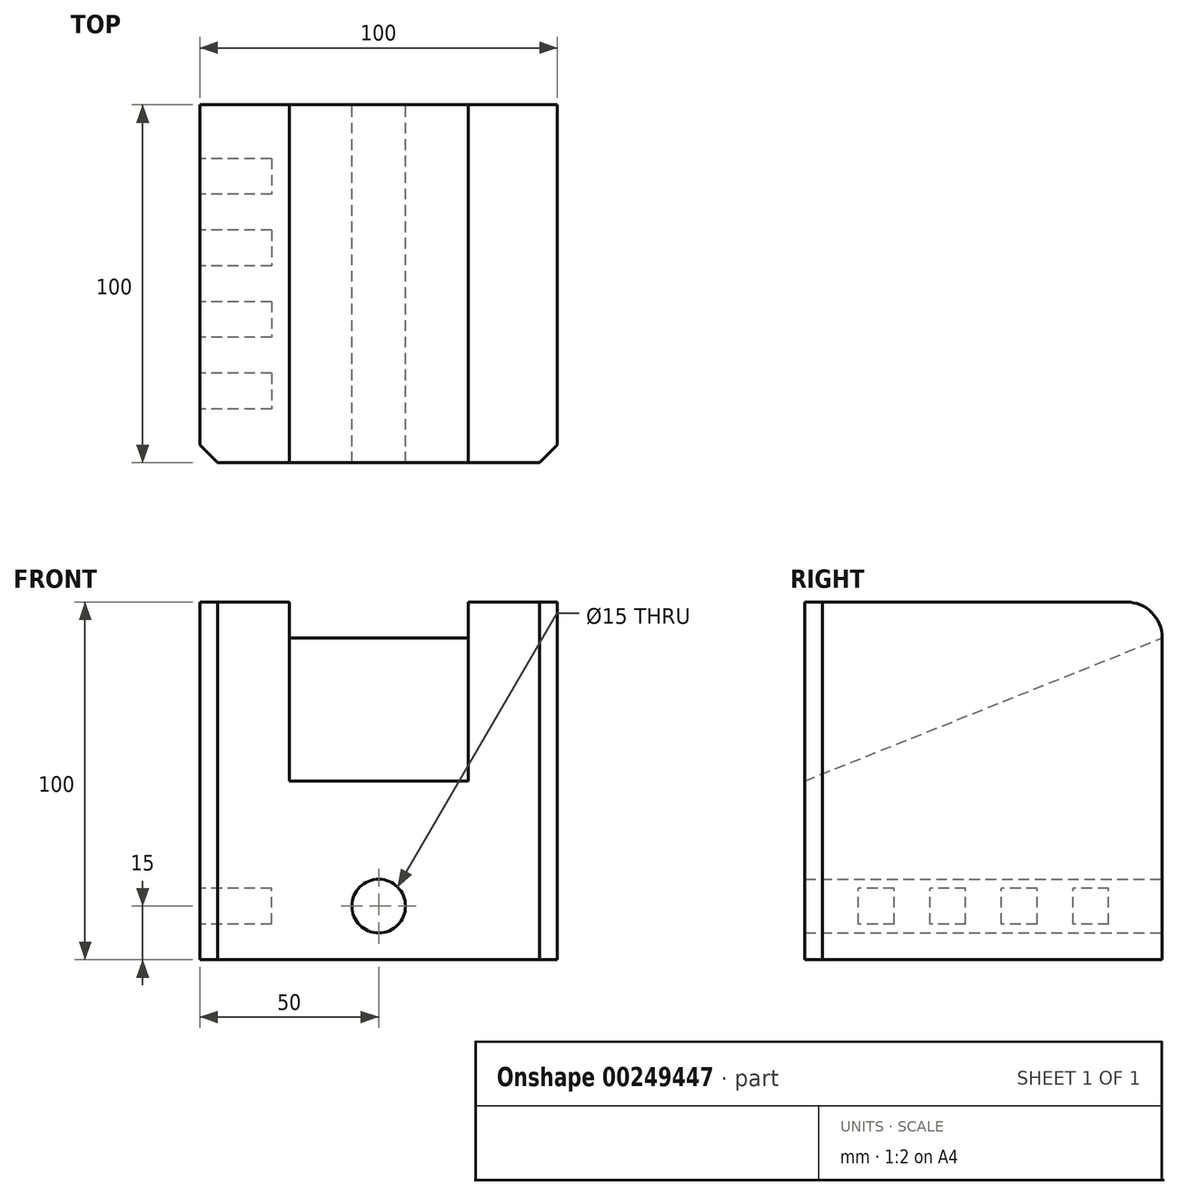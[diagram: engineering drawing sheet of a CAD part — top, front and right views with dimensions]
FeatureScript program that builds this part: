
annotation { "Feature Type Name" : "Feature", "Feature Type Description" : "" }
export const myFeature = defineFeature(function(context is Context, id is Id, definition is map)
    precondition{}
    {
        {
            var Q0;
            Q0=qCreatedBy(makeId("Front.planeOp"),FACE);
            var sketch = newSketch(context, id + "F0", { "sketchPlane" : qUnion([Q0])});
            skLineSegment(sketch, "E0.bottom", {"start": v(0, 0) * mm, "end": v(100, 0) * mm});
            skLineSegment(sketch, "E0.top", {"start": v(0, 100) * mm, "end": v(100, 100) * mm});
            skLineSegment(sketch, "E0.left", {"start": v(0, 0) * mm, "end": v(0, 100) * mm});
            skLineSegment(sketch, "E0.right", {"start": v(100, 0) * mm, "end": v(100, 100) * mm});
            skCircle(sketch, "E1", {"center": v(50, 15) * mm, "radius": 7.5 * mm});
            skSolve(sketch);
        }
        {
            var Q0;
            Q0=qSketchRegion(id+"F0",true);
            extrude(context, id + "F1", {"entities" : qUnion([Q0]), "depth" : 100 * mm});
        }
        {
            var Q0;
            Q0=makeQuery(id+"F1.opExtrude","SWEPT_FACE",FACE,{"disambiguationData":[OSD([sQuery(id+"F0.wireOp",EDGE,"E0.right")])]});
            var Q1;
            Q1=makeQuery(id+"F1.opExtrude","SWEPT_FACE",FACE,{"disambiguationData":[OSD([sQuery(id+"F0.wireOp",EDGE,"E0.left")])]});
            cPlane(context, id + "F2", {"entities" : qUnion([Q0, Q1]), "cplaneType" : CPlaneType.MID_PLANE, "offset" : 25 * mm, "width" : 150 * mm, "height" : 150 * mm});
        }
        {
            var Q0;
            Q0=qCreatedBy(id+"F2.planeOp",FACE);
            var sketch = newSketch(context, id + "F3", { "sketchPlane" : qUnion([Q0])});
            skLineSegment(sketch, "E2", {"start": v(0, 0) * mm, "end": v(0, 90) * mm, "construction": true});
            skLineSegment(sketch, "E3", {"start": v(0, 90) * mm, "end": v(0, 100) * mm});
            skLineSegment(sketch, "E4", {"start": v(0, 100) * mm, "end": v(-100, 100) * mm});
            skLineSegment(sketch, "E5", {"start": v(-100, 100) * mm, "end": v(-100, 50) * mm});
            skLineSegment(sketch, "E6", {"start": v(-100, 50) * mm, "end": v(0, 90) * mm});
            skSolve(sketch);
        }
        {
            var Q0;
            Q0=qSketchRegion(id+"F3",true);
            extrude(context, id + "F4", {"entities" : qUnion([Q0]), "operationType" : NewBodyOperationType.REMOVE, "endBound" : BoundingType.SYMMETRIC, "oppositeDirection" : true, "depth" : 50 * mm});
        }
        {
            var Q0;
            {var subQ0=sQuery(id+"F0.wireOp",EDGE,"E0.left");var subQ1=sQuery(id+"F0.wireOp",EDGE,"E0.top");Q0=makeQuery(id+"F4.boolean.opBoolean","SPLIT",EDGE,{"disambiguationData":[TD([makeQuery(id+"F1.opExtrude","SWEPT_FACE",FACE,{"disambiguationData":[OSD([subQ0])]})])],"derivedFrom":makeQuery(id+"F1.opExtrude","CAP_EDGE",EDGE,{"disambiguationData":[OSD([subQ1])],"isStart":true})});}
            var Q1;
            {var subQ0=sQuery(id+"F0.wireOp",EDGE,"E0.right");var subQ1=sQuery(id+"F0.wireOp",EDGE,"E0.top");Q1=makeQuery(id+"F4.boolean.opBoolean","SPLIT",EDGE,{"disambiguationData":[TD([makeQuery(id+"F1.opExtrude","SWEPT_FACE",FACE,{"disambiguationData":[OSD([subQ0])]})])],"derivedFrom":makeQuery(id+"F1.opExtrude","CAP_EDGE",EDGE,{"disambiguationData":[OSD([subQ1])],"isStart":true})});}
            fillet(context, id + "F5", {"entities" : qUnion([Q0, Q1]), "radius" : 10 * mm, "tangentPropagation" : true, "allowEdgeOverflow" : false});
        }
        {
            var Q0;
            Q0=makeQuery(id+"F1.opExtrude","CAP_EDGE",EDGE,{"disambiguationData":[OSD([sQuery(id+"F0.wireOp",EDGE,"E0.right")])],"isStart":false});
            var Q1;
            Q1=makeQuery(id+"F1.opExtrude","CAP_EDGE",EDGE,{"disambiguationData":[OSD([sQuery(id+"F0.wireOp",EDGE,"E0.left")])],"isStart":false});
            chamfer(context, id + "F6", {"entities" : qUnion([Q0, Q1]), "width" : 5 * mm, "tangentPropagation" : true});
        }
        {
            var Q0;
            Q0=qCreatedBy(makeId("Right.planeOp"),FACE);
            var sketch = newSketch(context, id + "F7", { "sketchPlane" : qUnion([Q0])});
            skLineSegment(sketch, "E7.bottom", {"start": v(-15, 10) * mm, "end": v(-25, 10) * mm});
            skLineSegment(sketch, "E7.top", {"start": v(-15, 20) * mm, "end": v(-25, 20) * mm});
            skLineSegment(sketch, "E7.left", {"start": v(-15, 10) * mm, "end": v(-15, 20) * mm});
            skLineSegment(sketch, "E7.right", {"start": v(-25, 10) * mm, "end": v(-25, 20) * mm});
            skLineSegment(sketch, "E8.1.0.0", {"start": v(-35, 20) * mm, "end": v(-45, 20) * mm});
            skLineSegment(sketch, "E8.1.0.1", {"start": v(-45, 10) * mm, "end": v(-45, 20) * mm});
            skLineSegment(sketch, "E8.1.0.2", {"start": v(-35, 10) * mm, "end": v(-45, 10) * mm});
            skLineSegment(sketch, "E8.1.0.3", {"start": v(-35, 10) * mm, "end": v(-35, 20) * mm});
            skLineSegment(sketch, "E8.2.0.0", {"start": v(-55, 20) * mm, "end": v(-65, 20) * mm});
            skLineSegment(sketch, "E8.2.0.1", {"start": v(-65, 10) * mm, "end": v(-65, 20) * mm});
            skLineSegment(sketch, "E8.2.0.2", {"start": v(-55, 10) * mm, "end": v(-65, 10) * mm});
            skLineSegment(sketch, "E8.2.0.3", {"start": v(-55, 10) * mm, "end": v(-55, 20) * mm});
            skLineSegment(sketch, "E8.3.0.0", {"start": v(-75, 20) * mm, "end": v(-85, 20) * mm});
            skLineSegment(sketch, "E8.3.0.1", {"start": v(-85, 10) * mm, "end": v(-85, 20) * mm});
            skLineSegment(sketch, "E8.3.0.2", {"start": v(-75, 10) * mm, "end": v(-85, 10) * mm});
            skLineSegment(sketch, "E8.3.0.3", {"start": v(-75, 10) * mm, "end": v(-75, 20) * mm});
            skLineSegment(sketch, "E8.direction1", {"start": v(-25, 20) * mm, "end": v(-45, 20) * mm, "construction": true});
            skSolve(sketch);
        }
        {
            var Q0;
            Q0=qSketchRegion(id+"F7",true);
            extrude(context, id + "F8", {"entities" : qUnion([Q0]), "operationType" : NewBodyOperationType.REMOVE, "depth" : 20 * mm});
        }
    });
